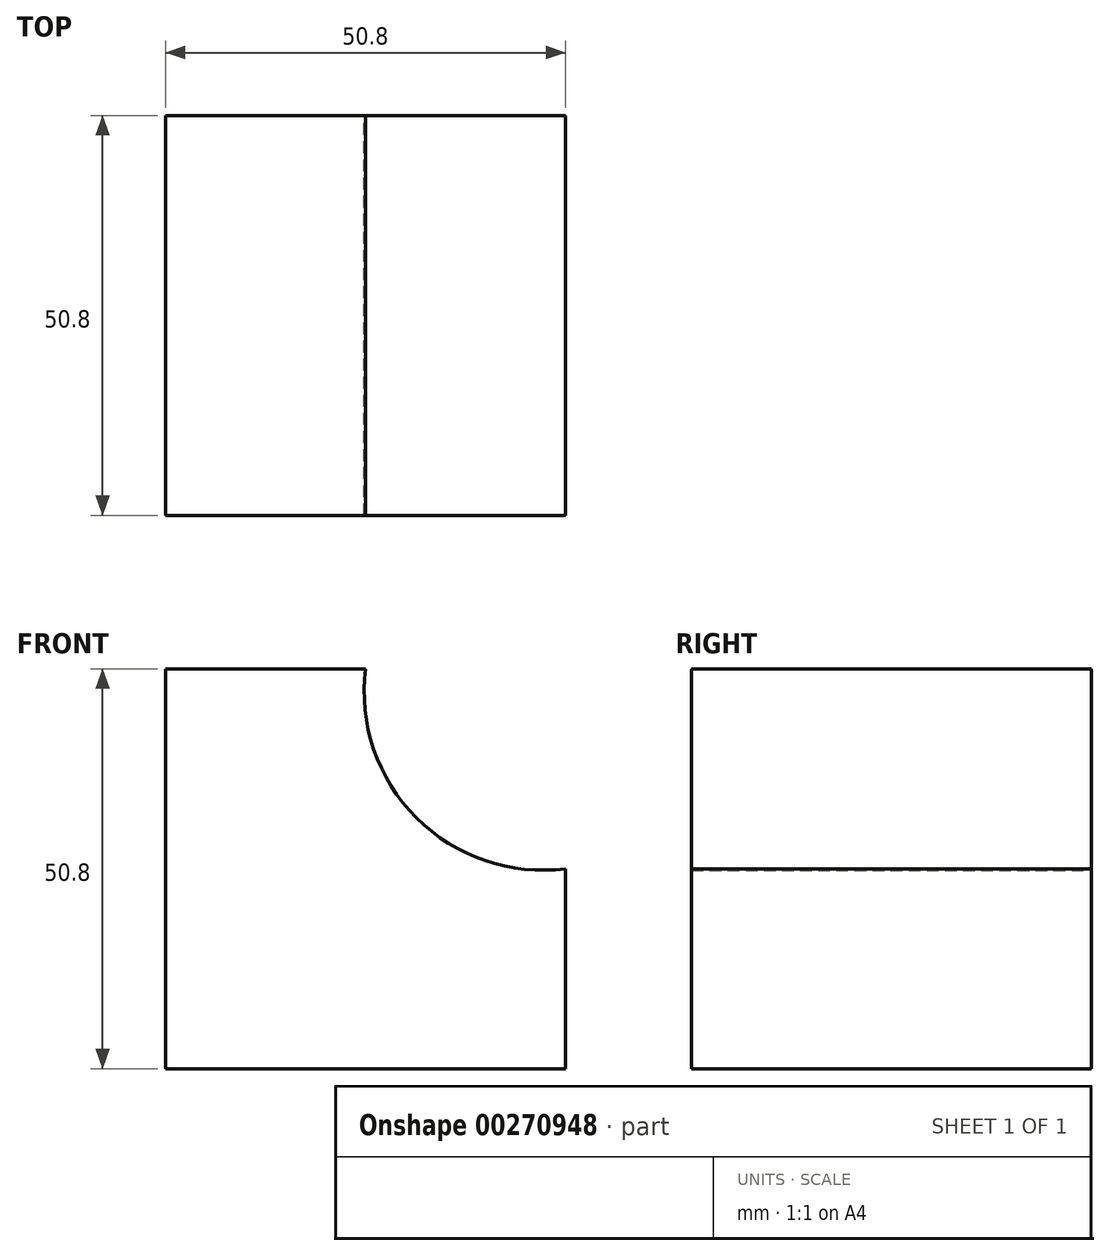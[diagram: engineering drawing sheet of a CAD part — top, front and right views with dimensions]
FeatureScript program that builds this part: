
annotation { "Feature Type Name" : "Feature", "Feature Type Description" : "" }
export const myFeature = defineFeature(function(context is Context, id is Id, definition is map)
    precondition{}
    {
        {
            var Q0;
            Q0=qCreatedBy(makeId("Front.planeOp"),FACE);
            var sketch = newSketch(context, id + "F0", { "sketchPlane" : qUnion([Q0])});
            skLineSegment(sketch, "E0", {"start": v(-65.12, 50.8) * mm, "end": v(-65.12, 0) * mm});
            skLineSegment(sketch, "E1", {"start": v(-65.12, 50.8) * mm, "end": v(-39.72, 50.8) * mm});
            skLineSegment(sketch, "E2", {"start": v(-65.12, 0) * mm, "end": v(-14.32, 0) * mm});
            skLineSegment(sketch, "E3", {"start": v(-14.32, 0) * mm, "end": v(-14.32, 25.4) * mm});
            skArc(sketch, "E4", {"start": v(-39.72, 50.8) * mm, "mid": v(-33.25, 31.86) * mm, "end": v(-14.32, 25.4) * mm});
            skSolve(sketch);
        }
        {
            var Q0;
            Q0 = qSketchRegion(id + "F0", true);
            extrude(context, id + "F1", {"entities" : qUnion([Q0]), "depth" : 50.8 * mm});
        }
    });
